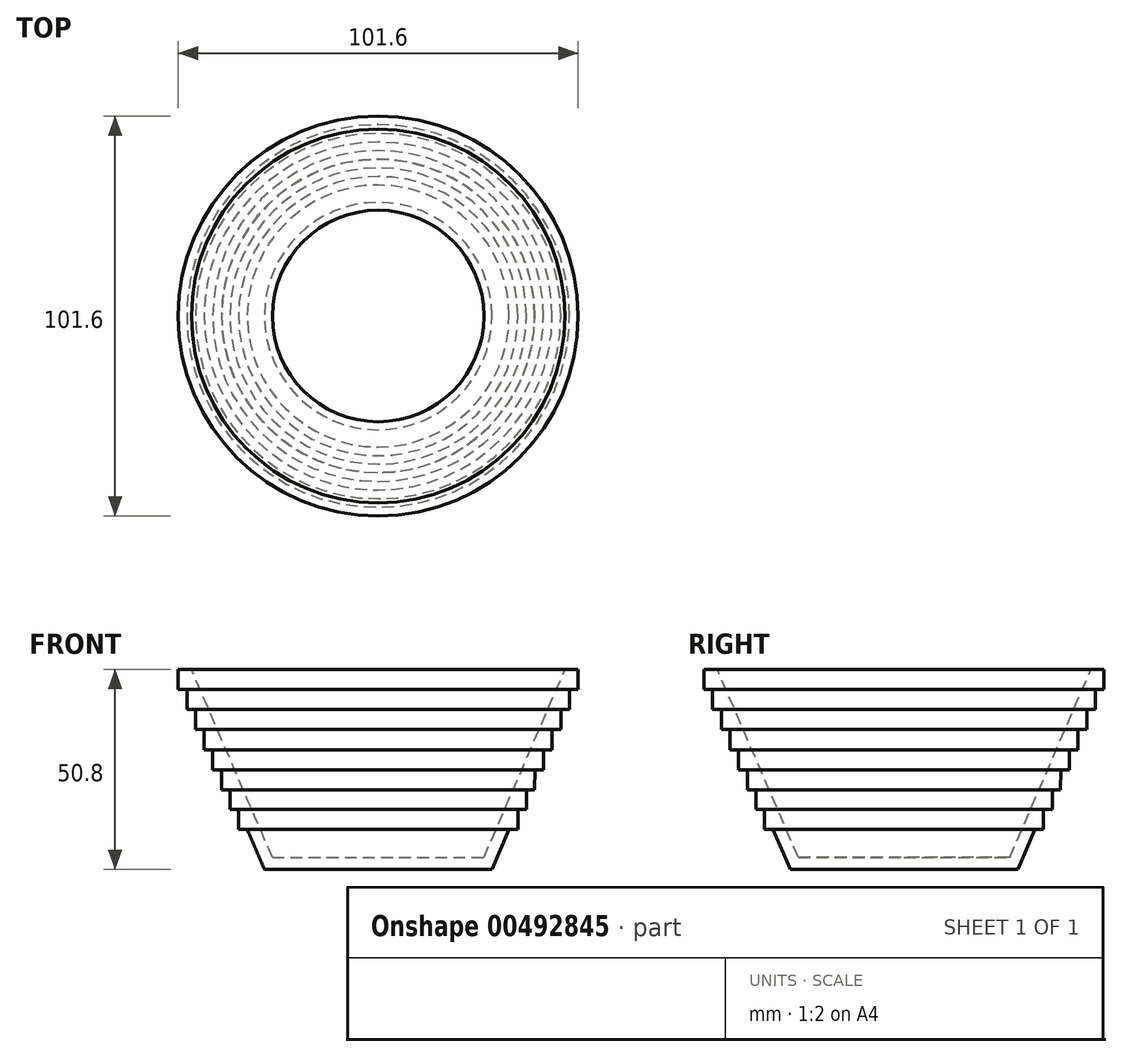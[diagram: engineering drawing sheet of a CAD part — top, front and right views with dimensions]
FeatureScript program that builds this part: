
annotation { "Feature Type Name" : "Feature", "Feature Type Description" : "" }
export const myFeature = defineFeature(function(context is Context, id is Id, definition is map)
    precondition{}
    {
        {
            var Q0;
            Q0=qCreatedBy(makeId("Front.planeOp"),FACE);
            var sketch = newSketch(context, id + "F0", { "sketchPlane" : qUnion([Q0])});
            skLineSegment(sketch, "E0", {"start": v(0, 0) * mm, "end": v(0, 50.8) * mm, "construction": true});
            skLineSegment(sketch, "E1", {"start": v(0, 0) * mm, "end": v(28.9, 0) * mm});
            skLineSegment(sketch, "E2", {"start": v(28.9, 0) * mm, "end": v(50.8, 50.8) * mm});
            skLineSegment(sketch, "E3.0", {"start": v(26.87, 3.07) * mm, "end": v(47.45, 50.8) * mm});
            skLineSegment(sketch, "E3.1", {"start": v(0, 3.07) * mm, "end": v(26.87, 3.07) * mm});
            skLineSegment(sketch, "E4", {"start": v(0, 50.8) * mm, "end": v(50.8, 50.8) * mm});
            skLineSegment(sketch, "E5", {"start": v(0, 3.07) * mm, "end": v(0, 0) * mm});
            skLineSegment(sketch, "E6", {"start": v(50.8, 50.8) * mm, "end": v(50.8, 45.72) * mm});
            skLineSegment(sketch, "E7", {"start": v(50.8, 45.72) * mm, "end": v(48.6, 45.72) * mm});
            skLineSegment(sketch, "E8", {"start": v(48.6, 45.72) * mm, "end": v(48.6, 40.62) * mm});
            skLineSegment(sketch, "E9", {"start": v(48.6, 40.62) * mm, "end": v(46.4, 40.62) * mm});
            skLineSegment(sketch, "E10", {"start": v(46.4, 40.62) * mm, "end": v(46.4, 35.52) * mm});
            skLineSegment(sketch, "E11", {"start": v(46.4, 35.52) * mm, "end": v(44.21, 35.52) * mm});
            skLineSegment(sketch, "E12", {"start": v(44.21, 35.52) * mm, "end": v(44.21, 30.42) * mm});
            skLineSegment(sketch, "E13", {"start": v(44.21, 30.42) * mm, "end": v(42.01, 30.42) * mm});
            skLineSegment(sketch, "E14", {"start": v(42.01, 30.42) * mm, "end": v(44.21, 30.42) * mm});
            skLineSegment(sketch, "E15", {"start": v(42.01, 30.42) * mm, "end": v(42.01, 25.34) * mm});
            skLineSegment(sketch, "E16", {"start": v(42.01, 25.34) * mm, "end": v(39.82, 25.34) * mm});
            skLineSegment(sketch, "E17", {"start": v(39.82, 25.34) * mm, "end": v(39.74, 20.27) * mm});
            skLineSegment(sketch, "E18", {"start": v(39.74, 20.27) * mm, "end": v(37.65, 20.3) * mm});
            skLineSegment(sketch, "E19", {"start": v(37.65, 20.3) * mm, "end": v(37.65, 15.23) * mm});
            skLineSegment(sketch, "E20", {"start": v(37.65, 15.23) * mm, "end": v(35.46, 15.23) * mm});
            skLineSegment(sketch, "E21", {"start": v(35.46, 15.23) * mm, "end": v(35.46, 10.17) * mm});
            skLineSegment(sketch, "E22", {"start": v(35.46, 10.17) * mm, "end": v(33.28, 10.17) * mm});
            skSolve(sketch);
        }
        {
            var Q0;
            Q0=makeQuery(id+"F0.imprint","IMPRINT",FACE,{"disambiguationData":[TD([[makeQuery(id+"F0.imprint","IMPRINT",EDGE,{"derivedFrom":sQuery(id+"F0.wireOp",EDGE,"E1")}),1.0]])]});
            var Q1;
            {var subQ0=sQuery(id+"F0.wireOp",EDGE,"E21");Q1=makeQuery(id+"F0.imprint","IMPRINT",FACE,{"disambiguationData":[TD([[makeQuery(id+"F0.imprint","IMPRINT",EDGE,{"derivedFrom":subQ0}),-1.0]])]});}
            var Q2;
            {var subQ0=sQuery(id+"F0.wireOp",EDGE,"E19");Q2=makeQuery(id+"F0.imprint","IMPRINT",FACE,{"disambiguationData":[TD([[makeQuery(id+"F0.imprint","IMPRINT",EDGE,{"derivedFrom":subQ0}),-1.0]])]});}
            var Q3;
            {var subQ0=sQuery(id+"F0.wireOp",EDGE,"E17");Q3=makeQuery(id+"F0.imprint","IMPRINT",FACE,{"disambiguationData":[TD([[makeQuery(id+"F0.imprint","IMPRINT",EDGE,{"derivedFrom":subQ0}),-1.0]])]});}
            var Q4;
            {var subQ0=sQuery(id+"F0.wireOp",EDGE,"E15");Q4=makeQuery(id+"F0.imprint","IMPRINT",FACE,{"disambiguationData":[TD([[makeQuery(id+"F0.imprint","IMPRINT",EDGE,{"derivedFrom":subQ0}),-1.0]])]});}
            var Q5;
            {var subQ0=sQuery(id+"F0.wireOp",EDGE,"E12");Q5=makeQuery(id+"F0.imprint","IMPRINT",FACE,{"disambiguationData":[TD([[makeQuery(id+"F0.imprint","IMPRINT",EDGE,{"derivedFrom":subQ0}),-1.0]])]});}
            var Q6;
            {var subQ0=sQuery(id+"F0.wireOp",EDGE,"E10");Q6=makeQuery(id+"F0.imprint","IMPRINT",FACE,{"disambiguationData":[TD([[makeQuery(id+"F0.imprint","IMPRINT",EDGE,{"derivedFrom":subQ0}),-1.0]])]});}
            var Q7;
            {var subQ0=sQuery(id+"F0.wireOp",EDGE,"E6");Q7=makeQuery(id+"F0.imprint","IMPRINT",FACE,{"disambiguationData":[TD([[makeQuery(id+"F0.imprint","IMPRINT",EDGE,{"derivedFrom":subQ0}),-1.0]])]});}
            var Q8;
            {var subQ0=sQuery(id+"F0.wireOp",EDGE,"E8");Q8=makeQuery(id+"F0.imprint","IMPRINT",FACE,{"disambiguationData":[TD([[makeQuery(id+"F0.imprint","IMPRINT",EDGE,{"derivedFrom":subQ0}),-1.0]])]});}
            var Q9;
            Q9=sQuery(id+"F0.wireOp",EDGE,"E0");
            revolve(context, id + "F1", {"entities" : qUnion([Q0, Q1, Q2, Q3, Q4, Q5, Q6, Q7, Q8]), "axis" : qUnion([Q9]), "revolveType" : RevolveType.FULL});
        }
    });
